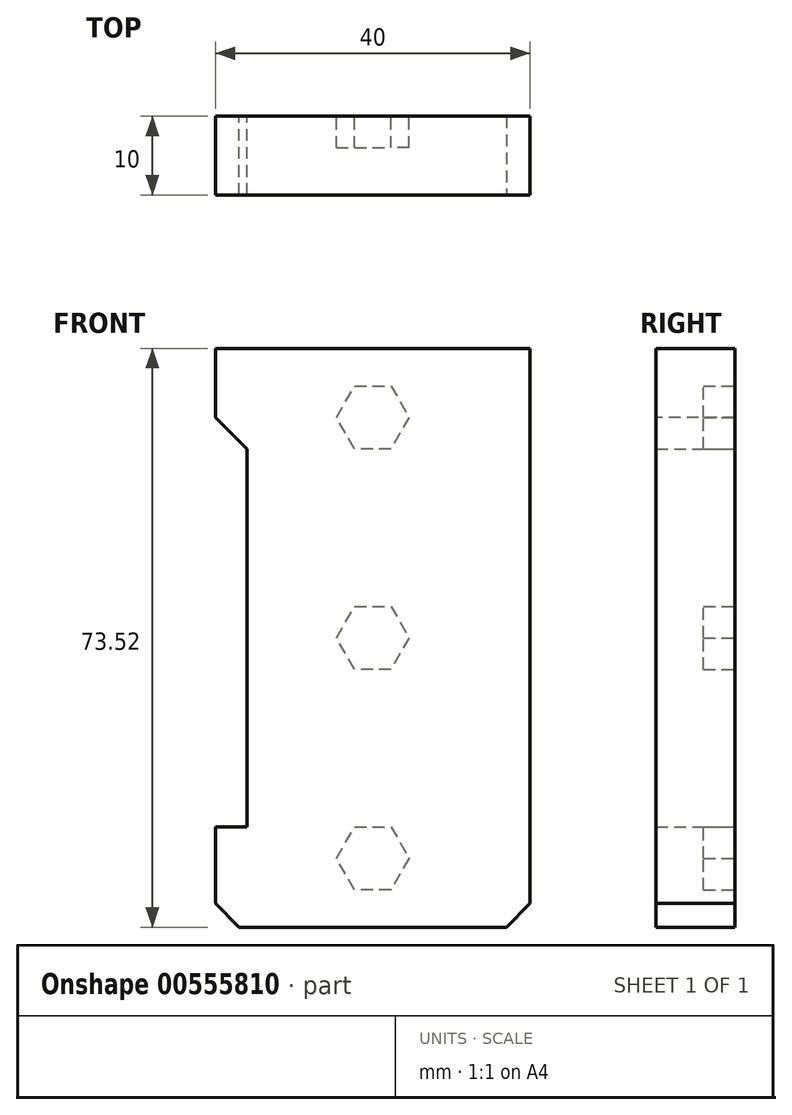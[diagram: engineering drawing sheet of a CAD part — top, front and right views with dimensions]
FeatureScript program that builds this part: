
annotation { "Feature Type Name" : "Feature", "Feature Type Description" : "" }
export const myFeature = defineFeature(function(context is Context, id is Id, definition is map)
    precondition{}
    {
        {
            var Q0;
            Q0=qCreatedBy(makeId("Front.planeOp"),FACE);
            var sketch = newSketch(context, id + "F0", { "sketchPlane" : qUnion([Q0])});
            skCircle(sketch, "E0.cCircle", {"center": v(0, 0) * mm, "radius": 4 * mm, "construction": true});
            skLineSegment(sketch, "E0.0", {"start": v(-2.3, 4) * mm, "end": v(2.3, 4) * mm});
            skLineSegment(sketch, "E0.1", {"start": v(2.3, 4) * mm, "end": v(4.62, 0) * mm});
            skLineSegment(sketch, "E0.2", {"start": v(4.62, 0) * mm, "end": v(2.3, -4) * mm});
            skLineSegment(sketch, "E0.3", {"start": v(2.3, -4) * mm, "end": v(-2.3, -4) * mm});
            skLineSegment(sketch, "E0.4", {"start": v(-2.3, -4) * mm, "end": v(-4.62, 0) * mm});
            skLineSegment(sketch, "E0.5", {"start": v(-4.62, 0) * mm, "end": v(-2.3, 4) * mm});
            skPoint(sketch, "E0.0.midPoint", {"position": v(0, 4) * mm});
            skCircle(sketch, "E1.cCircle", {"center": v(0, 28) * mm, "radius": 4 * mm, "construction": true});
            skLineSegment(sketch, "E1.0", {"start": v(-2.3, 32) * mm, "end": v(2.3, 32) * mm});
            skLineSegment(sketch, "E1.1", {"start": v(2.3, 32) * mm, "end": v(4.62, 28) * mm});
            skLineSegment(sketch, "E1.2", {"start": v(4.62, 28) * mm, "end": v(2.3, 24) * mm});
            skLineSegment(sketch, "E1.3", {"start": v(2.3, 24) * mm, "end": v(-2.3, 24) * mm});
            skLineSegment(sketch, "E1.4", {"start": v(-2.3, 24) * mm, "end": v(-4.62, 28) * mm});
            skLineSegment(sketch, "E1.5", {"start": v(-4.62, 28) * mm, "end": v(-2.3, 32) * mm});
            skPoint(sketch, "E1.0.midPoint", {"position": v(0, 32) * mm});
            skCircle(sketch, "E2.cCircle", {"center": v(0, -28) * mm, "radius": 4 * mm, "construction": true});
            skLineSegment(sketch, "E2.0", {"start": v(-2.3, -24) * mm, "end": v(2.3, -24) * mm});
            skLineSegment(sketch, "E2.1", {"start": v(2.3, -24) * mm, "end": v(4.62, -28) * mm});
            skLineSegment(sketch, "E2.2", {"start": v(4.62, -28) * mm, "end": v(2.3, -32) * mm});
            skLineSegment(sketch, "E2.3", {"start": v(2.3, -32) * mm, "end": v(-2.3, -32) * mm});
            skLineSegment(sketch, "E2.4", {"start": v(-2.3, -32) * mm, "end": v(-4.62, -28) * mm});
            skLineSegment(sketch, "E2.5", {"start": v(-4.62, -28) * mm, "end": v(-2.3, -24) * mm});
            skPoint(sketch, "E2.0.midPoint", {"position": v(0, -24) * mm});
            skSolve(sketch);
        }
        {
            var Q0;
            Q0=qCreatedBy(makeId("Front.planeOp"),FACE);
            var sketch = newSketch(context, id + "F1", { "sketchPlane" : qUnion([Q0])});
            skLineSegment(sketch, "E3.bottom", {"start": v(-20, 36.76) * mm, "end": v(20, 36.76) * mm});
            skLineSegment(sketch, "E3.top", {"start": v(-20, -36.76) * mm, "end": v(20, -36.76) * mm});
            skLineSegment(sketch, "E3.left", {"start": v(-20, 36.76) * mm, "end": v(-20, -36.76) * mm});
            skLineSegment(sketch, "E3.right", {"start": v(20, 36.76) * mm, "end": v(20, -36.76) * mm});
            skSolve(sketch);
        }
        {
            var Q0;
            Q0 = qSketchRegion(id + "F1", true);
            extrude(context, id + "F2", {"entities" : qUnion([Q0]), "depth" : 10 * mm, "offsetDistance" : 25 * mm});
        }
        {
            var Q0;
            Q0 = qSketchRegion(id + "F0", true);
            extrude(context, id + "F3", {"entities" : qUnion([Q0]), "operationType" : NewBodyOperationType.REMOVE, "depth" : 4 * mm, "offsetDistance" : 25 * mm});
        }
        {
            var Q0;
            Q0=makeQuery(id+"F2.opExtrude","SWEPT_EDGE",EDGE,{"disambiguationData":[OSD([sQuery(id+"F1.wireOp",EDGE,"E3.top"),sQuery(id+"F1.wireOp",EDGE,"E3.right")])]});
            chamfer(context, id + "F4", {"entities" : qUnion([Q0]), "width" : 3 * mm, "tangentPropagation" : true});
        }
        {
            var Q0;
            Q0=makeQuery(id+"F2.opExtrude","SWEPT_EDGE",EDGE,{"disambiguationData":[OSD([sQuery(id+"F1.wireOp",EDGE,"E3.top"),sQuery(id+"F1.wireOp",EDGE,"E3.left")])]});
            chamfer(context, id + "F5", {"entities" : qUnion([Q0]), "width" : 3 * mm, "tangentPropagation" : true});
        }
        {
            var Q0;
            Q0=qCreatedBy(makeId("Front.planeOp"),FACE);
            var sketch = newSketch(context, id + "F6", { "sketchPlane" : qUnion([Q0])});
            skLineSegment(sketch, "E4.bottom", {"start": v(-20, 24) * mm, "end": v(-16, 24) * mm});
            skLineSegment(sketch, "E4.top", {"start": v(-20, -24) * mm, "end": v(-16, -24) * mm});
            skLineSegment(sketch, "E4.left", {"start": v(-20, 24) * mm, "end": v(-20, -24) * mm});
            skLineSegment(sketch, "E4.right", {"start": v(-16, 24) * mm, "end": v(-16, -24) * mm});
            skSolve(sketch);
        }
        {
            var Q0;
            Q0 = qSketchRegion(id + "F6", true);
            extrude(context, id + "F7", {"entities" : qUnion([Q0]), "operationType" : NewBodyOperationType.REMOVE, "depth" : 25 * mm, "offsetDistance" : 25 * mm});
        }
        {
            var Q0;
            Q0=makeQuery(id+"F7.boolean.opBoolean","COPY",EDGE,{"derivedFrom":makeQuery(id+"F7.opExtrude","SWEPT_EDGE",EDGE,{"disambiguationData":[OSD([sQuery(id+"F6.wireOp",EDGE,"E4.bottom"),sQuery(id+"F6.wireOp",EDGE,"E4.left")])]})});
            var Q1;
            Q1=makeQuery(id+"F7.boolean.opBoolean","COPY",EDGE,{"derivedFrom":makeQuery(id+"F7.opExtrude","SWEPT_EDGE",EDGE,{"disambiguationData":[OSD([sQuery(id+"F6.wireOp",EDGE,"E4.top"),sQuery(id+"F6.wireOp",EDGE,"E4.left")])]})});
            chamfer(context, id + "F8", {"entities" : qUnion([Q0, Q1]), "width" : 4 * mm, "tangentPropagation" : true});
        }
    });
